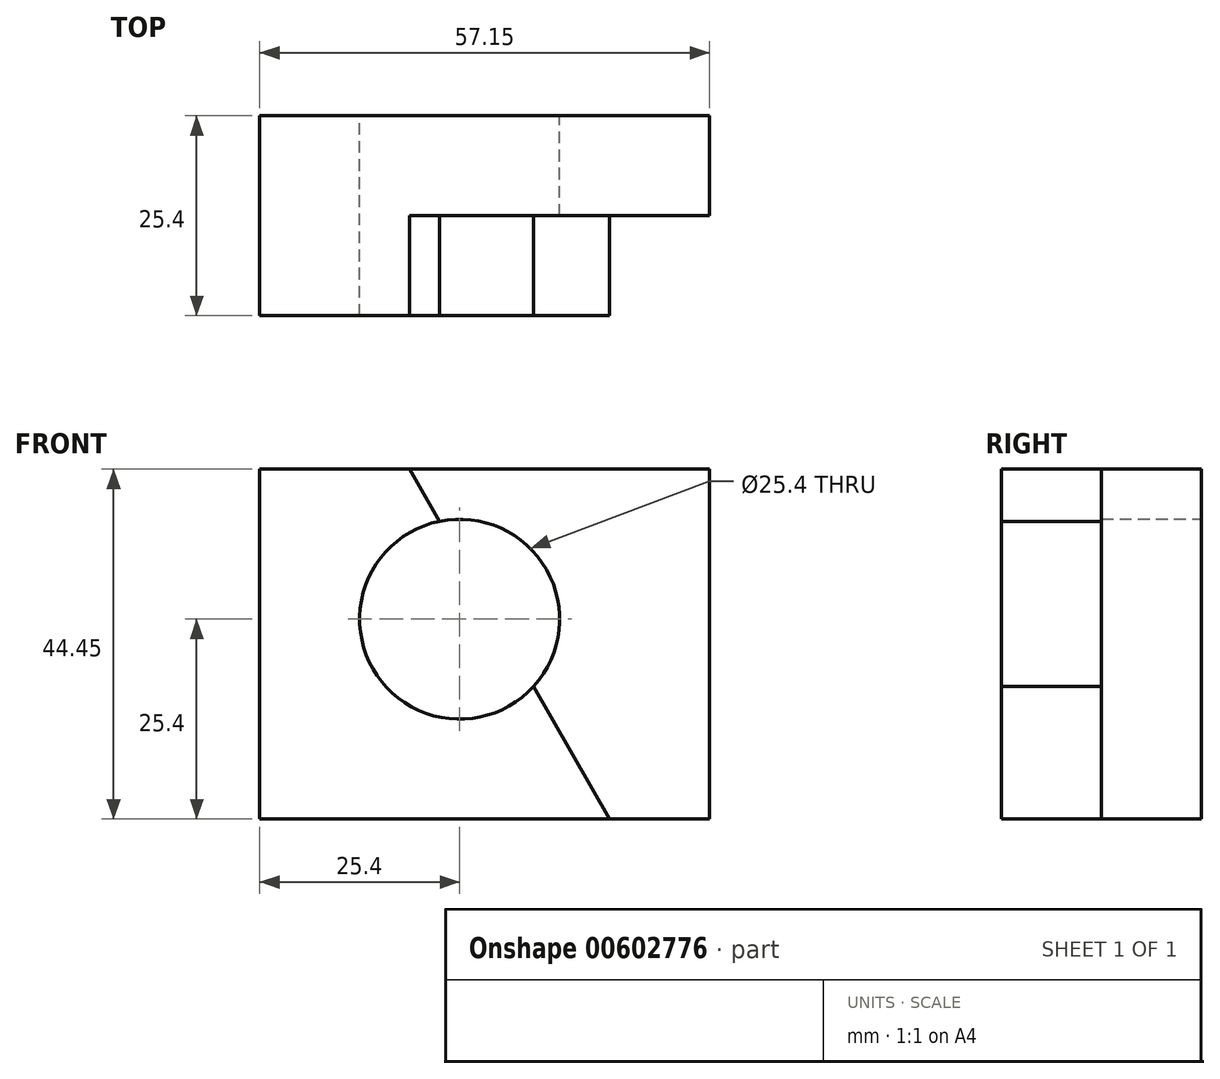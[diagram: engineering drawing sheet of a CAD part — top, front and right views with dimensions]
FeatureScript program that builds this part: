
annotation { "Feature Type Name" : "Feature", "Feature Type Description" : "" }
export const myFeature = defineFeature(function(context is Context, id is Id, definition is map)
    precondition{}
    {
        {
            var Q0;
            Q0=qCreatedBy(makeId("Front.planeOp"),FACE);
            var sketch = newSketch(context, id + "F0", { "sketchPlane" : qUnion([Q0])});
            skLineSegment(sketch, "E0", {"start": v(0, 0) * mm, "end": v(0, 44.45) * mm});
            skLineSegment(sketch, "E1", {"start": v(0, 44.45) * mm, "end": v(57.15, 44.45) * mm});
            skLineSegment(sketch, "E2", {"start": v(57.15, 44.45) * mm, "end": v(57.15, 0) * mm});
            skLineSegment(sketch, "E3", {"start": v(57.15, 0) * mm, "end": v(0, 0) * mm});
            skCircle(sketch, "E4", {"center": v(25.4, 25.4) * mm, "radius": 12.7 * mm});
            skSolve(sketch);
        }
        {
            var Q0;
            Q0=makeQuery(id+"F0.imprint","IMPRINT",FACE,{"disambiguationData":[TD([[makeQuery(id+"F0.imprint","IMPRINT",EDGE,{"derivedFrom":sQuery(id+"F0.wireOp",EDGE,"E0")}),-1.0]])]});
            extrude(context, id + "F1", {"entities" : qUnion([Q0]), "depth" : 25.4 * mm, "offsetDistance" : 25.4 * mm});
        }
        {
            var Q0;
            Q0=makeQuery(id+"F1.opExtrude","CAP_FACE",FACE,{"disambiguationData":[OSD([sQuery(id+"F0.wireOp",EDGE,"E0"),sQuery(id+"F0.wireOp",EDGE,"E1"),sQuery(id+"F0.wireOp",EDGE,"E2"),sQuery(id+"F0.wireOp",EDGE,"E3"),sQuery(id+"F0.wireOp",EDGE,"E4")])],"isStart":false});
            var sketch = newSketch(context, id + "F2", { "sketchPlane" : qUnion([Q0])});
            skLineSegment(sketch, "E5", {"start": v(0, 44.45) * mm, "end": v(19.05, 44.45) * mm});
            skLineSegment(sketch, "E6", {"start": v(57.15, 0) * mm, "end": v(44.45, 0) * mm});
            skLineSegment(sketch, "E7", {"start": v(44.45, 0) * mm, "end": v(19.05, 44.45) * mm});
            skSolve(sketch);
        }
        {
            var Q0;
            Q0=makeQuery(id+"F2.imprint","IMPRINT",FACE,{"disambiguationData":[TD([[makeQuery(id+"F2.imprint","IMPRINT",EDGE,{"derivedFrom":sQuery(id+"F2.wireOp",EDGE,"E6")}),-1.0]])]});
            extrude(context, id + "F3", {"entities" : qUnion([Q0]), "operationType" : NewBodyOperationType.REMOVE, "oppositeDirection" : true, "depth" : 12.7 * mm, "offsetDistance" : 25.4 * mm});
        }
    });
